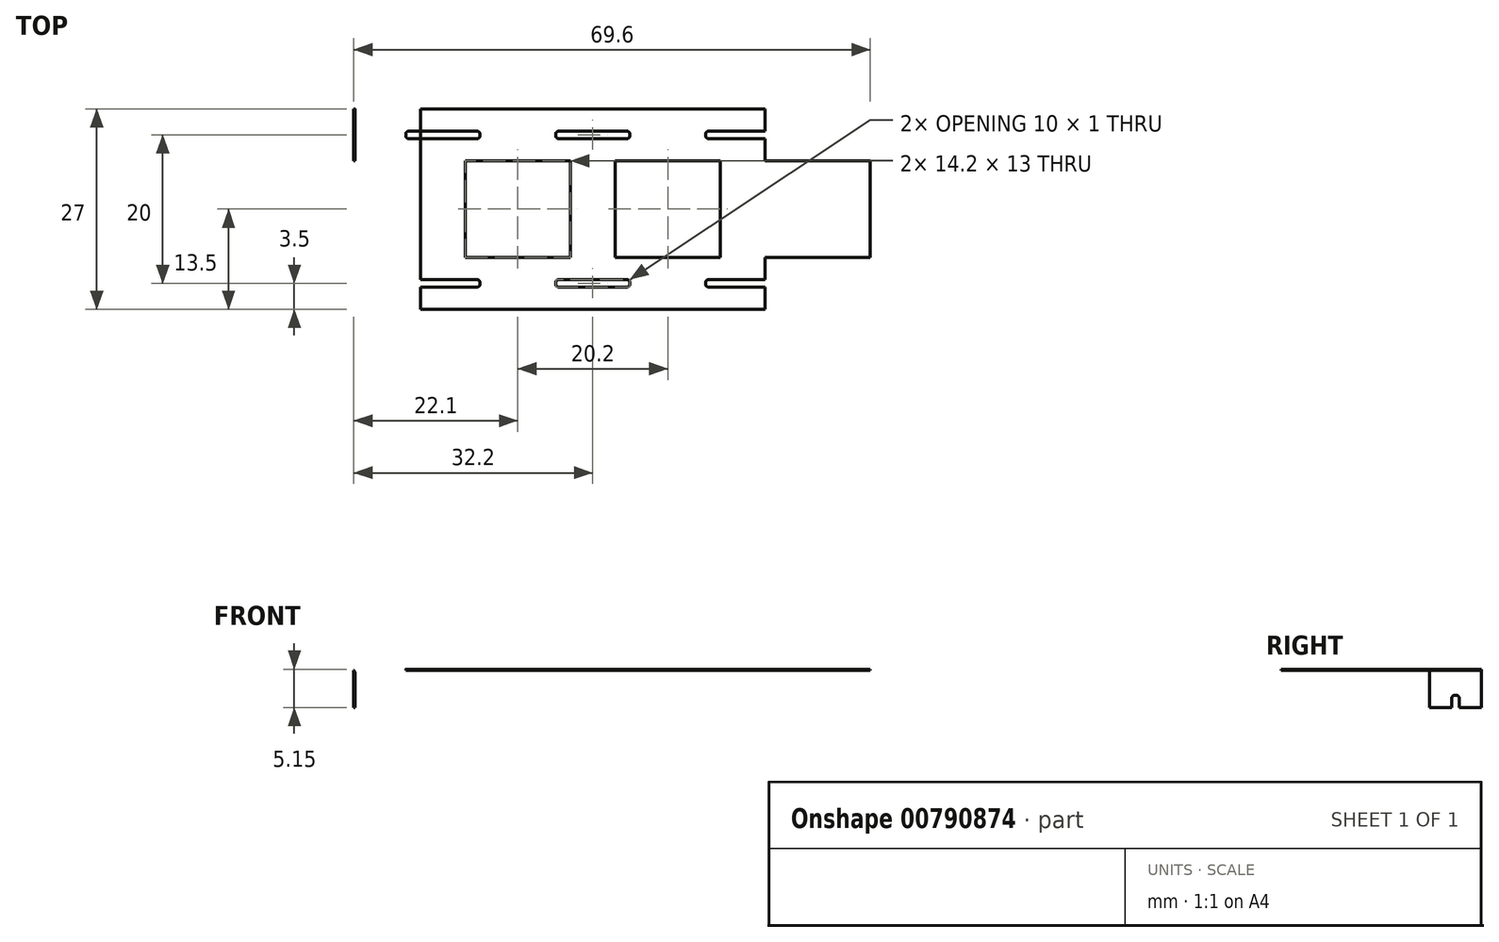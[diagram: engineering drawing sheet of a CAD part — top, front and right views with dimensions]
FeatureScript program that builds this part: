
annotation { "Feature Type Name" : "Feature", "Feature Type Description" : "" }
export const myFeature = defineFeature(function(context is Context, id is Id, definition is map)
    precondition{}
    {
        {
            var Q0;
            Q0=qCreatedBy(makeId("Top.planeOp"),FACE);
            var sketch = newSketch(context, id + "F0", { "sketchPlane" : qUnion([Q0])});
            skLineSegment(sketch, "E0.bottom", {"start": v(7.1, 6.5) * mm, "end": v(-7.1, 6.5) * mm});
            skLineSegment(sketch, "E0.top", {"start": v(7.1, -6.5) * mm, "end": v(-7.1, -6.5) * mm});
            skLineSegment(sketch, "E0.left", {"start": v(7.1, 6.5) * mm, "end": v(7.1, -6.5) * mm});
            skLineSegment(sketch, "E0.right", {"start": v(-7.1, 6.5) * mm, "end": v(-7.1, -6.5) * mm});
            skPoint(sketch, "E0.middle", {"position": v(0, 0) * mm});
            skLineSegment(sketch, "E1", {"start": v(13.1, 13.5) * mm, "end": v(13.1, 10.5) * mm});
            skLineSegment(sketch, "E2", {"start": v(13.1, 13.5) * mm, "end": v(-7.1, 13.5) * mm});
            skLineSegment(sketch, "E3.bottom", {"start": v(5.5, 9.5) * mm, "end": v(14.7, 9.5) * mm});
            skLineSegment(sketch, "E3.top", {"start": v(5.5, 10.5) * mm, "end": v(14.7, 10.5) * mm});
            skLineSegment(sketch, "E3.left", {"start": v(5.1, 9.9) * mm, "end": v(5.1, 10.1) * mm});
            skLineSegment(sketch, "E3.right", {"start": v(15.1, 9.9) * mm, "end": v(15.1, 10.1) * mm});
            skPoint(sketch, "E3.middle", {"position": v(10.1, 10) * mm});
            skPoint(sketch, "E4.visualSharp", {"position": v(5.1, 10.5) * mm});
            skArc(sketch, "E4.filletArc", {"start": v(5.5, 10.5) * mm, "mid": v(5.22, 10.38) * mm, "end": v(5.1, 10.1) * mm});
            skPoint(sketch, "E5.visualSharp", {"position": v(5.1, 9.5) * mm});
            skArc(sketch, "E5.filletArc", {"start": v(5.1, 9.9) * mm, "mid": v(5.22, 9.62) * mm, "end": v(5.5, 9.5) * mm});
            skPoint(sketch, "E6.visualSharp", {"position": v(15.1, 10.5) * mm});
            skArc(sketch, "E6.filletArc", {"start": v(15.1, 10.1) * mm, "mid": v(14.98, 10.38) * mm, "end": v(14.7, 10.5) * mm});
            skPoint(sketch, "E7.visualSharp", {"position": v(15.1, 9.5) * mm});
            skArc(sketch, "E7.filletArc", {"start": v(14.7, 9.5) * mm, "mid": v(14.98, 9.62) * mm, "end": v(15.1, 9.9) * mm});
            skLineSegment(sketch, "E8.trimOffspring", {"start": v(13.1, 9.5) * mm, "end": v(13.1, 0) * mm});
            skArc(sketch, "E9.MirrorCS", {"start": v(-5.5, 10.5) * mm, "mid": v(-5.22, 10.38) * mm, "end": v(-5.1, 10.1) * mm});
            skArc(sketch, "E10.MirrorCS", {"start": v(-15.1, 10.1) * mm, "mid": v(-14.98, 10.38) * mm, "end": v(-14.7, 10.5) * mm});
            skLineSegment(sketch, "E11.MirrorCS", {"start": v(-15.1, 9.9) * mm, "end": v(-15.1, 10.1) * mm});
            skArc(sketch, "E12.MirrorCS", {"start": v(-14.7, 9.5) * mm, "mid": v(-14.98, 9.62) * mm, "end": v(-15.1, 9.9) * mm});
            skArc(sketch, "E13.MirrorCS", {"start": v(-5.1, 9.9) * mm, "mid": v(-5.22, 9.62) * mm, "end": v(-5.5, 9.5) * mm});
            skLineSegment(sketch, "E14.MirrorCS", {"start": v(-5.1, 9.9) * mm, "end": v(-5.1, 10.1) * mm});
            skPoint(sketch, "E15.MirrorP", {"position": v(-5.1, 9.5) * mm});
            skLineSegment(sketch, "E16.MirrorCS", {"start": v(-5.5, 10.5) * mm, "end": v(-14.7, 10.5) * mm});
            skPoint(sketch, "E17.MirrorP", {"position": v(-10.1, 10) * mm});
            skLineSegment(sketch, "E18.MirrorCS", {"start": v(-5.5, 9.5) * mm, "end": v(-14.7, 9.5) * mm});
            skPoint(sketch, "E19.MirrorP", {"position": v(-15.1, 10.5) * mm});
            skLineSegment(sketch, "E20.MirrorCS", {"start": v(-13.1, 9.5) * mm, "end": v(-13.1, 0) * mm});
            skPoint(sketch, "E21.MirrorP", {"position": v(-5.1, 10.5) * mm});
            skLineSegment(sketch, "E22.MirrorCS", {"start": v(-13.1, 13.5) * mm, "end": v(-13.1, 10.5) * mm});
            skPoint(sketch, "E23.MirrorP", {"position": v(-15.1, 9.5) * mm});
            skLineSegment(sketch, "E24", {"start": v(-13.1, 13.5) * mm, "end": v(-7.1, 13.5) * mm});
            skLineSegment(sketch, "E25.bottom", {"start": v(-13.1, 13.5) * mm, "end": v(-22.1, 13.5) * mm});
            skLineSegment(sketch, "E25.top", {"start": v(-13.1, 6.5) * mm, "end": v(-22.1, 6.5) * mm});
            skLineSegment(sketch, "E25.left", {"start": v(-13.1, 13.5) * mm, "end": v(-13.1, 6.5) * mm});
            skLineSegment(sketch, "E25.right", {"start": v(-22.1, 13.5) * mm, "end": v(-22.1, 6.5) * mm});
            skArc(sketch, "E26.MirrorCS", {"start": v(14.7, -9.5) * mm, "mid": v(14.98, -9.62) * mm, "end": v(15.1, -9.9) * mm});
            skLineSegment(sketch, "E27.MirrorCS", {"start": v(15.1, -9.9) * mm, "end": v(15.1, -10.1) * mm});
            skArc(sketch, "E28.MirrorCS", {"start": v(15.1, -10.1) * mm, "mid": v(14.98, -10.38) * mm, "end": v(14.7, -10.5) * mm});
            skLineSegment(sketch, "E29.MirrorCS", {"start": v(13.1, -13.5) * mm, "end": v(13.1, -10.5) * mm});
            skLineSegment(sketch, "E30.MirrorCS", {"start": v(13.1, -9.5) * mm, "end": v(13.1, 0) * mm});
            skLineSegment(sketch, "E31.MirrorCS", {"start": v(13.1, -13.5) * mm, "end": v(-7.1, -13.5) * mm});
            skLineSegment(sketch, "E32.MirrorCS", {"start": v(5.5, -10.5) * mm, "end": v(14.7, -10.5) * mm});
            skPoint(sketch, "E33.MirrorP", {"position": v(15.1, -9.5) * mm});
            skPoint(sketch, "E34.MirrorP", {"position": v(15.1, -10.5) * mm});
            skPoint(sketch, "E35.MirrorP", {"position": v(10.1, -10) * mm});
            skLineSegment(sketch, "E36.MirrorCS", {"start": v(5.5, -9.5) * mm, "end": v(14.7, -9.5) * mm});
            skLineSegment(sketch, "E37.MirrorCS", {"start": v(5.1, -9.9) * mm, "end": v(5.1, -10.1) * mm});
            skArc(sketch, "E38.MirrorCS", {"start": v(5.1, -9.9) * mm, "mid": v(5.22, -9.62) * mm, "end": v(5.5, -9.5) * mm});
            skArc(sketch, "E39.MirrorCS", {"start": v(5.5, -10.5) * mm, "mid": v(5.22, -10.38) * mm, "end": v(5.1, -10.1) * mm});
            skPoint(sketch, "E40.MirrorP", {"position": v(5.1, -10.5) * mm});
            skPoint(sketch, "E41.MirrorP", {"position": v(5.1, -9.5) * mm});
            skArc(sketch, "E42.MirrorCS", {"start": v(-5.1, -9.9) * mm, "mid": v(-5.22, -9.62) * mm, "end": v(-5.5, -9.5) * mm});
            skArc(sketch, "E43.MirrorCS", {"start": v(-5.5, -10.5) * mm, "mid": v(-5.22, -10.38) * mm, "end": v(-5.1, -10.1) * mm});
            skLineSegment(sketch, "E44.MirrorCS", {"start": v(-5.1, -9.9) * mm, "end": v(-5.1, -10.1) * mm});
            skPoint(sketch, "E45.MirrorP", {"position": v(-5.1, -10.5) * mm});
            skLineSegment(sketch, "E46.MirrorCS", {"start": v(-5.5, -10.5) * mm, "end": v(-13.1, -10.5) * mm});
            skPoint(sketch, "E47.MirrorP", {"position": v(-10.1, -10) * mm});
            skPoint(sketch, "E48.MirrorP", {"position": v(-5.1, -9.5) * mm});
            skLineSegment(sketch, "E49.MirrorCS", {"start": v(-5.5, -9.5) * mm, "end": v(-13.1, -9.5) * mm});
            skLineSegment(sketch, "E50.MirrorCS", {"start": v(-13.1, -13.5) * mm, "end": v(-13.1, -10.5) * mm});
            skLineSegment(sketch, "E51.MirrorCS", {"start": v(-13.1, -13.5) * mm, "end": v(-7.1, -13.5) * mm});
            skLineSegment(sketch, "E52.MirrorCS", {"start": v(-13.1, -9.5) * mm, "end": v(-13.1, 0) * mm});
            skLineSegment(sketch, "E53.1.0.0", {"start": v(33.3, 9.5) * mm, "end": v(33.3, 0) * mm});
            skPoint(sketch, "E53.1.0.1", {"position": v(25.3, -9.5) * mm});
            skLineSegment(sketch, "E53.1.0.2", {"start": v(33.3, -9.5) * mm, "end": v(33.3, 0) * mm});
            skLineSegment(sketch, "E53.1.0.3", {"start": v(33.3, -13.5) * mm, "end": v(13.1, -13.5) * mm});
            skPoint(sketch, "E53.1.0.4", {"position": v(20.2, 0) * mm});
            skLineSegment(sketch, "E53.1.0.5", {"start": v(27.3, 6.5) * mm, "end": v(27.3, -6.5) * mm});
            skLineSegment(sketch, "E53.1.0.6", {"start": v(27.3, -6.5) * mm, "end": v(13.1, -6.5) * mm});
            skLineSegment(sketch, "E53.1.0.7", {"start": v(27.3, 6.5) * mm, "end": v(13.1, 6.5) * mm});
            skPoint(sketch, "E53.1.0.8", {"position": v(30.3, 10) * mm});
            skPoint(sketch, "E53.1.0.9", {"position": v(25.3, 10.5) * mm});
            skLineSegment(sketch, "E53.1.0.10", {"start": v(25.7, -9.5) * mm, "end": v(34.9, -9.5) * mm});
            skPoint(sketch, "E53.1.0.11", {"position": v(30.3, -10) * mm});
            skPoint(sketch, "E53.1.0.12", {"position": v(25.3, -10.5) * mm});
            skLineSegment(sketch, "E53.1.0.13", {"start": v(25.7, 10.5) * mm, "end": v(34.9, 10.5) * mm});
            skPoint(sketch, "E53.1.0.14", {"position": v(25.3, 9.5) * mm});
            skLineSegment(sketch, "E53.1.0.15", {"start": v(33.3, 13.5) * mm, "end": v(33.3, 10.5) * mm});
            skLineSegment(sketch, "E53.1.0.16", {"start": v(33.3, -13.5) * mm, "end": v(33.3, -10.5) * mm});
            skLineSegment(sketch, "E53.1.0.17", {"start": v(25.7, 9.5) * mm, "end": v(34.9, 9.5) * mm});
            skLineSegment(sketch, "E53.1.0.18", {"start": v(33.3, 13.5) * mm, "end": v(13.1, 13.5) * mm});
            skPoint(sketch, "E53.1.0.19", {"position": v(35.3, -10.5) * mm});
            skLineSegment(sketch, "E53.1.0.20", {"start": v(25.7, -10.5) * mm, "end": v(34.9, -10.5) * mm});
            skPoint(sketch, "E53.1.0.21", {"position": v(35.3, 9.5) * mm});
            skPoint(sketch, "E53.1.0.22", {"position": v(35.3, 10.5) * mm});
            skPoint(sketch, "E53.1.0.23", {"position": v(35.3, -9.5) * mm});
            skPoint(sketch, "E53.1.0.24", {"position": v(20.2, 0) * mm});
            skArc(sketch, "E53.1.0.25", {"start": v(35.3, 10.1) * mm, "mid": v(35.18, 10.38) * mm, "end": v(34.9, 10.5) * mm});
            skArc(sketch, "E53.1.0.26", {"start": v(34.9, 9.5) * mm, "mid": v(35.18, 9.62) * mm, "end": v(35.3, 9.9) * mm});
            skArc(sketch, "E53.1.0.27", {"start": v(25.3, 9.9) * mm, "mid": v(25.42, 9.62) * mm, "end": v(25.7, 9.5) * mm});
            skArc(sketch, "E53.1.0.28", {"start": v(25.7, 10.5) * mm, "mid": v(25.42, 10.38) * mm, "end": v(25.3, 10.1) * mm});
            skLineSegment(sketch, "E53.1.0.29", {"start": v(35.3, 9.9) * mm, "end": v(35.3, 10.1) * mm});
            skLineSegment(sketch, "E53.1.0.30", {"start": v(25.3, 9.9) * mm, "end": v(25.3, 10.1) * mm});
            skArc(sketch, "E53.1.0.31", {"start": v(25.7, -10.5) * mm, "mid": v(25.42, -10.38) * mm, "end": v(25.3, -10.1) * mm});
            skArc(sketch, "E53.1.0.32", {"start": v(25.3, -9.9) * mm, "mid": v(25.42, -9.62) * mm, "end": v(25.7, -9.5) * mm});
            skArc(sketch, "E53.1.0.33", {"start": v(34.9, -9.5) * mm, "mid": v(35.18, -9.62) * mm, "end": v(35.3, -9.9) * mm});
            skArc(sketch, "E53.1.0.34", {"start": v(35.3, -10.1) * mm, "mid": v(35.18, -10.38) * mm, "end": v(34.9, -10.5) * mm});
            skLineSegment(sketch, "E53.1.0.35", {"start": v(35.3, -9.9) * mm, "end": v(35.3, -10.1) * mm});
            skLineSegment(sketch, "E53.1.0.36", {"start": v(25.3, -9.9) * mm, "end": v(25.3, -10.1) * mm});
            skLineSegment(sketch, "E53.1.0.37", {"start": v(13.1, 6.5) * mm, "end": v(13.1, -6.5) * mm});
            skLineSegment(sketch, "E53.2.0.0", {"start": v(53.5, 9.5) * mm, "end": v(53.5, 0) * mm});
            skPoint(sketch, "E53.2.0.1", {"position": v(45.5, -9.5) * mm});
            skLineSegment(sketch, "E53.2.0.2", {"start": v(53.5, -9.5) * mm, "end": v(53.5, 0) * mm});
            skLineSegment(sketch, "E53.2.0.3", {"start": v(53.5, -13.5) * mm, "end": v(33.3, -13.5) * mm});
            skPoint(sketch, "E53.2.0.4", {"position": v(40.4, 0) * mm});
            skLineSegment(sketch, "E53.2.0.5", {"start": v(47.5, 6.5) * mm, "end": v(47.5, -6.5) * mm});
            skLineSegment(sketch, "E53.2.0.6", {"start": v(47.5, -6.5) * mm, "end": v(33.3, -6.5) * mm});
            skLineSegment(sketch, "E53.2.0.7", {"start": v(47.5, 6.5) * mm, "end": v(33.3, 6.5) * mm});
            skPoint(sketch, "E53.2.0.8", {"position": v(50.5, 10) * mm});
            skPoint(sketch, "E53.2.0.9", {"position": v(45.5, 10.5) * mm});
            skLineSegment(sketch, "E53.2.0.10", {"start": v(45.9, -9.5) * mm, "end": v(55.1, -9.5) * mm});
            skPoint(sketch, "E53.2.0.11", {"position": v(50.5, -10) * mm});
            skPoint(sketch, "E53.2.0.12", {"position": v(45.5, -10.5) * mm});
            skLineSegment(sketch, "E53.2.0.13", {"start": v(45.9, 10.5) * mm, "end": v(55.1, 10.5) * mm});
            skPoint(sketch, "E53.2.0.14", {"position": v(45.5, 9.5) * mm});
            skLineSegment(sketch, "E53.2.0.15", {"start": v(53.5, 13.5) * mm, "end": v(53.5, 10.5) * mm});
            skLineSegment(sketch, "E53.2.0.16", {"start": v(53.5, -13.5) * mm, "end": v(53.5, -10.5) * mm});
            skLineSegment(sketch, "E53.2.0.17", {"start": v(45.9, 9.5) * mm, "end": v(55.1, 9.5) * mm});
            skLineSegment(sketch, "E53.2.0.18", {"start": v(53.5, 13.5) * mm, "end": v(33.3, 13.5) * mm});
            skPoint(sketch, "E53.2.0.19", {"position": v(55.5, -10.5) * mm});
            skLineSegment(sketch, "E53.2.0.20", {"start": v(45.9, -10.5) * mm, "end": v(55.1, -10.5) * mm});
            skPoint(sketch, "E53.2.0.21", {"position": v(55.5, 9.5) * mm});
            skPoint(sketch, "E53.2.0.22", {"position": v(55.5, 10.5) * mm});
            skPoint(sketch, "E53.2.0.23", {"position": v(55.5, -9.5) * mm});
            skPoint(sketch, "E53.2.0.24", {"position": v(40.4, 0) * mm});
            skArc(sketch, "E53.2.0.25", {"start": v(55.5, 10.1) * mm, "mid": v(55.38, 10.38) * mm, "end": v(55.1, 10.5) * mm});
            skArc(sketch, "E53.2.0.26", {"start": v(55.1, 9.5) * mm, "mid": v(55.38, 9.62) * mm, "end": v(55.5, 9.9) * mm});
            skArc(sketch, "E53.2.0.27", {"start": v(45.5, 9.9) * mm, "mid": v(45.62, 9.62) * mm, "end": v(45.9, 9.5) * mm});
            skArc(sketch, "E53.2.0.28", {"start": v(45.9, 10.5) * mm, "mid": v(45.62, 10.38) * mm, "end": v(45.5, 10.1) * mm});
            skLineSegment(sketch, "E53.2.0.29", {"start": v(55.5, 9.9) * mm, "end": v(55.5, 10.1) * mm});
            skLineSegment(sketch, "E53.2.0.30", {"start": v(45.5, 9.9) * mm, "end": v(45.5, 10.1) * mm});
            skArc(sketch, "E53.2.0.31", {"start": v(45.9, -10.5) * mm, "mid": v(45.62, -10.38) * mm, "end": v(45.5, -10.1) * mm});
            skArc(sketch, "E53.2.0.32", {"start": v(45.5, -9.9) * mm, "mid": v(45.62, -9.62) * mm, "end": v(45.9, -9.5) * mm});
            skArc(sketch, "E53.2.0.33", {"start": v(55.1, -9.5) * mm, "mid": v(55.38, -9.62) * mm, "end": v(55.5, -9.9) * mm});
            skArc(sketch, "E53.2.0.34", {"start": v(55.5, -10.1) * mm, "mid": v(55.38, -10.38) * mm, "end": v(55.1, -10.5) * mm});
            skLineSegment(sketch, "E53.2.0.35", {"start": v(55.5, -9.9) * mm, "end": v(55.5, -10.1) * mm});
            skLineSegment(sketch, "E53.2.0.36", {"start": v(45.5, -9.9) * mm, "end": v(45.5, -10.1) * mm});
            skLineSegment(sketch, "E53.2.0.37", {"start": v(33.3, 6.5) * mm, "end": v(33.3, -6.5) * mm});
            skLineSegment(sketch, "E53.direction1", {"start": v(-7.1, -13.5) * mm, "end": v(13.1, -13.5) * mm, "construction": true});
            skPoint(sketch, "E54.orphan", {"position": v(-14.7, -9.5) * mm});
            skPoint(sketch, "E55.orphan", {"position": v(-14.7, -10.5) * mm});
            skLineSegment(sketch, "E56.trimOffspring", {"start": v(-13.1, -9.5) * mm, "end": v(-13.1, -6.5) * mm});
            skSolve(sketch);
        }
        {
            var Q0;
            {var subQ5=sQuery(id+"F0.wireOp",EDGE,"E10.MirrorCS");Q0=makeQuery(id+"F0.imprint","IMPRINT",FACE,{"disambiguationData":[TD([[makeQuery(id+"F0.imprint","IMPRINT",EDGE,{"derivedFrom":subQ5}),1.0]])]});}
            var Q1;
            {var subQ14=sQuery(id+"F0.wireOp",EDGE,"E53.1.0.0");Q1=makeQuery(id+"F0.imprint","IMPRINT",FACE,{"disambiguationData":[TD([[makeQuery(id+"F0.imprint","IMPRINT",EDGE,{"derivedFrom":subQ14}),1.0]])]});}
            var Q2;
            Q2=makeQuery(id+"F0.imprint","IMPRINT",FACE,{"disambiguationData":[TD([[makeQuery(id+"F0.imprint","IMPRINT",EDGE,{"derivedFrom":sQuery(id+"F0.wireOp",EDGE,"E0.bottom")}),-1.0]])]});
            var Q3;
            {var subQ5=sQuery(id+"F0.wireOp",EDGE,"E1");Q3=makeQuery(id+"F0.imprint","IMPRINT",FACE,{"disambiguationData":[TD([[makeQuery(id+"F0.imprint","IMPRINT",EDGE,{"derivedFrom":subQ5}),1.0]])]});}
            extrude(context, id + "F1", {"entities" : qUnion([Q0, Q1, Q2, Q3]), "depth" : 0.15 * mm, "offsetDistance" : 25 * mm});
        }
        {
            var Q0;
            Q0=makeQuery(id+"F1.opExtrude","CAP_FACE",FACE,{"disambiguationData":[OSD([sQuery(id+"F0.wireOp",EDGE,"E0.bottom"),sQuery(id+"F0.wireOp",EDGE,"E0.top"),sQuery(id+"F0.wireOp",EDGE,"E0.left"),sQuery(id+"F0.wireOp",EDGE,"E0.right"),sQuery(id+"F0.wireOp",EDGE,"E2"),sQuery(id+"F0.wireOp",EDGE,"E3.bottom"),sQuery(id+"F0.wireOp",EDGE,"E3.top"),sQuery(id+"F0.wireOp",EDGE,"E3.left"),sQuery(id+"F0.wireOp",EDGE,"E3.right"),sQuery(id+"F0.wireOp",EDGE,"E4.filletArc"),sQuery(id+"F0.wireOp",EDGE,"E5.filletArc"),sQuery(id+"F0.wireOp",EDGE,"E6.filletArc"),sQuery(id+"F0.wireOp",EDGE,"E7.filletArc"),sQuery(id+"F0.wireOp",EDGE,"E9.MirrorCS"),sQuery(id+"F0.wireOp",EDGE,"E10.MirrorCS"),sQuery(id+"F0.wireOp",EDGE,"E11.MirrorCS"),sQuery(id+"F0.wireOp",EDGE,"E12.MirrorCS"),sQuery(id+"F0.wireOp",EDGE,"E13.MirrorCS"),sQuery(id+"F0.wireOp",EDGE,"E14.MirrorCS"),sQuery(id+"F0.wireOp",EDGE,"E16.MirrorCS"),sQuery(id+"F0.wireOp",EDGE,"E18.MirrorCS"),sQuery(id+"F0.wireOp",EDGE,"E20.MirrorCS"),sQuery(id+"F0.wireOp",EDGE,"E24"),sQuery(id+"F0.wireOp",EDGE,"E25.bottom"),sQuery(id+"F0.wireOp",EDGE,"E25.top"),sQuery(id+"F0.wireOp",EDGE,"E25.right"),sQuery(id+"F0.wireOp",EDGE,"E26.MirrorCS"),sQuery(id+"F0.wireOp",EDGE,"E27.MirrorCS"),sQuery(id+"F0.wireOp",EDGE,"E28.MirrorCS"),sQuery(id+"F0.wireOp",EDGE,"E31.MirrorCS"),sQuery(id+"F0.wireOp",EDGE,"E32.MirrorCS"),sQuery(id+"F0.wireOp",EDGE,"E36.MirrorCS"),sQuery(id+"F0.wireOp",EDGE,"E37.MirrorCS"),sQuery(id+"F0.wireOp",EDGE,"E38.MirrorCS"),sQuery(id+"F0.wireOp",EDGE,"E39.MirrorCS"),sQuery(id+"F0.wireOp",EDGE,"E42.MirrorCS"),sQuery(id+"F0.wireOp",EDGE,"E43.MirrorCS"),sQuery(id+"F0.wireOp",EDGE,"E44.MirrorCS"),sQuery(id+"F0.wireOp",EDGE,"E46.MirrorCS"),sQuery(id+"F0.wireOp",EDGE,"E49.MirrorCS"),sQuery(id+"F0.wireOp",EDGE,"E50.MirrorCS"),sQuery(id+"F0.wireOp",EDGE,"E51.MirrorCS"),sQuery(id+"F0.wireOp",EDGE,"E52.MirrorCS"),sQuery(id+"F0.wireOp",EDGE,"E53.1.0.3"),sQuery(id+"F0.wireOp",EDGE,"E53.1.0.5"),sQuery(id+"F0.wireOp",EDGE,"E53.1.0.6"),sQuery(id+"F0.wireOp",EDGE,"E53.1.0.7"),sQuery(id+"F0.wireOp",EDGE,"E53.1.0.10"),sQuery(id+"F0.wireOp",EDGE,"E53.1.0.13"),sQuery(id+"F0.wireOp",EDGE,"E53.1.0.17"),sQuery(id+"F0.wireOp",EDGE,"E53.1.0.18"),sQuery(id+"F0.wireOp",EDGE,"E53.1.0.20"),sQuery(id+"F0.wireOp",EDGE,"E53.1.0.25"),sQuery(id+"F0.wireOp",EDGE,"E53.1.0.26"),sQuery(id+"F0.wireOp",EDGE,"E53.1.0.27"),sQuery(id+"F0.wireOp",EDGE,"E53.1.0.28"),sQuery(id+"F0.wireOp",EDGE,"E53.1.0.29"),sQuery(id+"F0.wireOp",EDGE,"E53.1.0.30"),sQuery(id+"F0.wireOp",EDGE,"E53.1.0.31"),sQuery(id+"F0.wireOp",EDGE,"E53.1.0.32"),sQuery(id+"F0.wireOp",EDGE,"E53.1.0.33"),sQuery(id+"F0.wireOp",EDGE,"E53.1.0.34"),sQuery(id+"F0.wireOp",EDGE,"E53.1.0.35"),sQuery(id+"F0.wireOp",EDGE,"E53.1.0.36"),sQuery(id+"F0.wireOp",EDGE,"E53.1.0.37"),sQuery(id+"F0.wireOp",EDGE,"E53.2.0.0"),sQuery(id+"F0.wireOp",EDGE,"E53.2.0.2"),sQuery(id+"F0.wireOp",EDGE,"E53.2.0.3"),sQuery(id+"F0.wireOp",EDGE,"E53.2.0.5"),sQuery(id+"F0.wireOp",EDGE,"E53.2.0.6"),sQuery(id+"F0.wireOp",EDGE,"E53.2.0.7"),sQuery(id+"F0.wireOp",EDGE,"E53.2.0.10"),sQuery(id+"F0.wireOp",EDGE,"E53.2.0.13"),sQuery(id+"F0.wireOp",EDGE,"E53.2.0.15"),sQuery(id+"F0.wireOp",EDGE,"E53.2.0.16"),sQuery(id+"F0.wireOp",EDGE,"E53.2.0.17"),sQuery(id+"F0.wireOp",EDGE,"E53.2.0.18"),sQuery(id+"F0.wireOp",EDGE,"E53.2.0.20"),sQuery(id+"F0.wireOp",EDGE,"E53.2.0.27"),sQuery(id+"F0.wireOp",EDGE,"E53.2.0.28"),sQuery(id+"F0.wireOp",EDGE,"E53.2.0.30"),sQuery(id+"F0.wireOp",EDGE,"E53.2.0.31"),sQuery(id+"F0.wireOp",EDGE,"E53.2.0.32"),sQuery(id+"F0.wireOp",EDGE,"E53.2.0.36"),sQuery(id+"F0.wireOp",EDGE,"E53.2.0.37"),sQuery(id+"F0.wireOp",EDGE,"E56.trimOffspring")])],"isStart":true});
            var sketch = newSketch(context, id + "F2", { "sketchPlane" : qUnion([Q0])});
            skLineSegment(sketch, "E57.bottom", {"start": v(-22.1, -13.5) * mm, "end": v(-21.95, -13.5) * mm});
            skLineSegment(sketch, "E57.top", {"start": v(-22.1, -6.5) * mm, "end": v(-21.95, -6.5) * mm});
            skLineSegment(sketch, "E57.left", {"start": v(-22.1, -13.5) * mm, "end": v(-22.1, -6.5) * mm});
            skLineSegment(sketch, "E57.right", {"start": v(-21.95, -13.5) * mm, "end": v(-21.95, -6.5) * mm});
            skSolve(sketch);
        }
        {
            var Q0;
            Q0 = qSketchRegion(id + "F2", true);
            extrude(context, id + "F3", {"entities" : qUnion([Q0]), "operationType" : NewBodyOperationType.ADD, "depth" : 5 * mm, "offsetDistance" : 25 * mm});
        }
        {
            var Q0;
            Q0=makeQuery(id+"F3.opExtrude","CAP_EDGE",EDGE,{"disambiguationData":[OSD([sQuery(id+"F2.wireOp",EDGE,"E57.right")])],"isStart":true});
            var Q1;
            Q1=makeQuery(id+"F1.opExtrude","CAP_EDGE",EDGE,{"disambiguationData":[OSD([sQuery(id+"F0.wireOp",EDGE,"E25.right")])],"isStart":false});
            fillet(context, id + "F4", {"entities" : qUnion([Q0, Q1]), "radius" : 0.5 * mm, "tangentPropagation" : true, "allowEdgeOverflow" : false});
        }
        {
            var Q0;
            Q0=makeQuery(id+"F3.boolean.opBoolean","MERGE",FACE,{"derivedFrom":[makeQuery(id+"F1.opExtrude","SWEPT_FACE",FACE,{"disambiguationData":[OSD([sQuery(id+"F0.wireOp",EDGE,"E25.right")])]}),makeQuery(id+"F3.opExtrude","SWEPT_FACE",FACE,{"disambiguationData":[OSD([sQuery(id+"F2.wireOp",EDGE,"E57.left")])]})]});
            var sketch = newSketch(context, id + "F5", { "sketchPlane" : qUnion([Q0])});
            skLineSegment(sketch, "E58", {"start": v(-10, -0.35) * mm, "end": v(-10, -3.35) * mm});
            skLineSegment(sketch, "E59", {"start": v(-10, -3.35) * mm, "end": v(-9.9, -3.35) * mm});
            skLineSegment(sketch, "E60", {"start": v(-9.5, -3.75) * mm, "end": v(-9.5, -5) * mm});
            skPoint(sketch, "E61.visualSharp", {"position": v(-9.5, -3.35) * mm});
            skArc(sketch, "E61.filletArc", {"start": v(-9.5, -3.75) * mm, "mid": v(-9.62, -3.47) * mm, "end": v(-9.9, -3.35) * mm});
            skPoint(sketch, "E62.MirrorP", {"position": v(-10.5, -3.35) * mm});
            skLineSegment(sketch, "E63.MirrorCS", {"start": v(-10.5, -3.75) * mm, "end": v(-10.5, -5) * mm});
            skArc(sketch, "E64.MirrorCS", {"start": v(-10.5, -3.75) * mm, "mid": v(-10.38, -3.47) * mm, "end": v(-10.1, -3.35) * mm});
            skLineSegment(sketch, "E65.MirrorCS", {"start": v(-10, -3.35) * mm, "end": v(-10.1, -3.35) * mm});
            skSolve(sketch);
        }
        {
            var Q0;
            Q0=makeQuery(id+"F5.imprint","IMPRINT",FACE,{"disambiguationData":[TD([[makeQuery(id+"F5.imprint","IMPRINT",EDGE,{"derivedFrom":sQuery(id+"F5.wireOp",EDGE,"E59")}),-1.0]])]});
            extrude(context, id + "F6", {"entities" : qUnion([Q0]), "operationType" : NewBodyOperationType.REMOVE, "oppositeDirection" : true, "depth" : 25 * mm, "offsetDistance" : 25 * mm});
        }
    });
